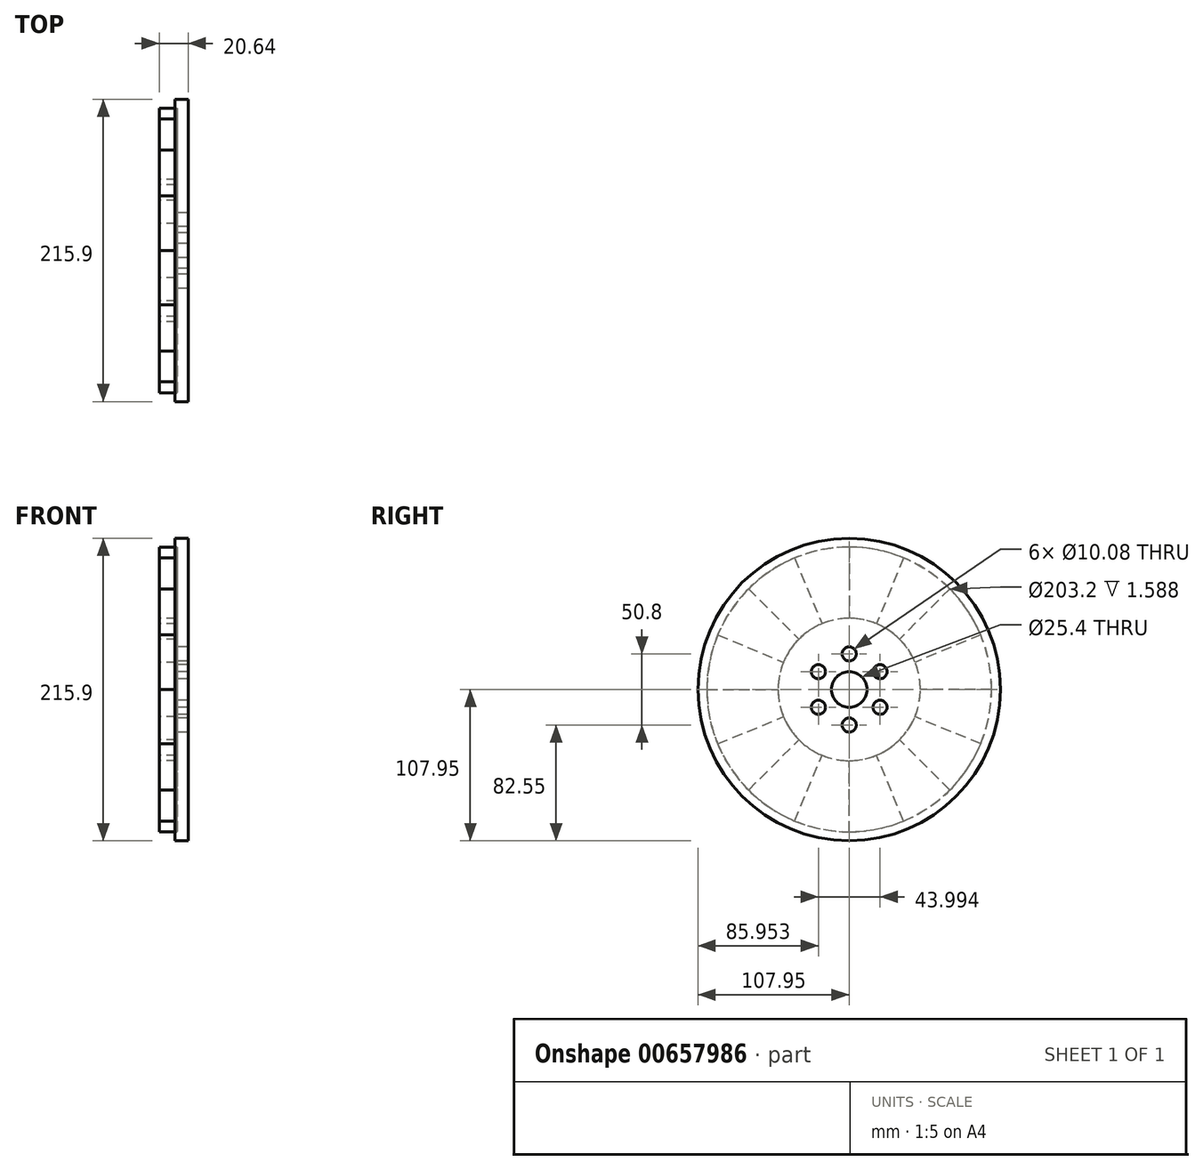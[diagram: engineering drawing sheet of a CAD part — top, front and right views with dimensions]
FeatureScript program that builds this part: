
annotation { "Feature Type Name" : "Feature", "Feature Type Description" : "" }
export const myFeature = defineFeature(function(context is Context, id is Id, definition is map)
    precondition{}
    {
        {
            var Q0;
            Q0=qCreatedBy(makeId("Front.planeOp"),FACE);
            var sketch = newSketch(context, id + "F0", { "sketchPlane" : qUnion([Q0])});
            skLineSegment(sketch, "E0", {"start": v(-9.52, 12.7) * mm, "end": v(0, 12.7) * mm});
            skLineSegment(sketch, "E1", {"start": v(0, 12.7) * mm, "end": v(0, 107.95) * mm});
            skLineSegment(sketch, "E2", {"start": v(0, 107.95) * mm, "end": v(-9.52, 107.95) * mm});
            skLineSegment(sketch, "E3", {"start": v(-9.52, 107.95) * mm, "end": v(-9.52, 101.6) * mm});
            skLineSegment(sketch, "E4", {"start": v(-9.52, 101.6) * mm, "end": v(-7.94, 101.6) * mm});
            skLineSegment(sketch, "E5", {"start": v(-7.94, 101.6) * mm, "end": v(-7.94, 50.8) * mm});
            skLineSegment(sketch, "E6", {"start": v(-7.94, 50.8) * mm, "end": v(-9.52, 50.8) * mm});
            skLineSegment(sketch, "E7", {"start": v(-9.52, 50.8) * mm, "end": v(-9.52, 12.7) * mm});
            skLineSegment(sketch, "E8", {"start": v(-50.8, 0) * mm, "end": v(50.8, 0) * mm, "construction": true});
            skLineSegment(sketch, "E9", {"start": v(0, 0) * mm, "end": v(0, 12.7) * mm, "construction": true});
            skLineSegment(sketch, "E10.bottom", {"start": v(-20.64, 101.6) * mm, "end": v(-7.94, 101.6) * mm});
            skLineSegment(sketch, "E10.top", {"start": v(-20.64, 50.8) * mm, "end": v(-7.94, 50.8) * mm});
            skLineSegment(sketch, "E10.left", {"start": v(-20.64, 101.6) * mm, "end": v(-20.64, 50.8) * mm});
            skSolve(sketch);
        }
        {
            var Q0;
            Q0=makeQuery(id+"F0.imprint","IMPRINT",FACE,{"disambiguationData":[TD([[makeQuery(id+"F0.imprint","IMPRINT",EDGE,{"derivedFrom":sQuery(id+"F0.wireOp",EDGE,"E0")}),1.0]])]});
            var Q1;
            Q1=sQuery(id+"F0.wireOp",EDGE,"E8");
            revolve(context, id + "F1", {"entities" : qUnion([Q0]), "axis" : qUnion([Q1]), "revolveType" : RevolveType.FULL});
        }
        {
            var Q0;
            {var subQ3=sQuery(id+"F0.wireOp",EDGE,"E10.left");Q0=makeQuery(id+"F0.imprint","IMPRINT",FACE,{"disambiguationData":[TD([[makeQuery(id+"F0.imprint","IMPRINT",EDGE,{"derivedFrom":subQ3}),1.0]])]});}
            var Q1;
            Q1=sQuery(id+"F0.wireOp",EDGE,"E8");
            revolve(context, id + "F2", {"entities" : qUnion([Q0]), "axis" : qUnion([Q1]), "revolveType" : RevolveType.ONE_DIRECTION, "angle" : 22.5 * degree});
        }
        {
            var Q0;
            Q0=makeQuery(id+"F2.opRevolve","SWEPT_BODY",BODY,{"disambiguationData":[OSD([sQuery(id+"F0.wireOp",EDGE,"E10.bottom"),sQuery(id+"F0.wireOp",EDGE,"E10.top"),sQuery(id+"F0.wireOp",EDGE,"E10.left"),sQuery(id+"F0.wireOp",EDGE,"E5")])]});
            var Q1;
            Q1=sQuery(id+"F0.wireOp",EDGE,"E8");
            circularPattern(context, id + "F3", {"entities" : qUnion([Q0]), "axis" : qUnion([Q1]), "angle" : 360 * degree, "instanceCount" : 16, "equalSpace" : true});
        }
        {
            var Q0;
            Q0=makeQuery(id+"F1.opRevolve","SWEPT_FACE",FACE,{"disambiguationData":[OSD([sQuery(id+"F0.wireOp",EDGE,"E7")])]});
            var sketch = newSketch(context, id + "F4", { "sketchPlane" : qUnion([Q0])});
            skCircle(sketch, "E11.cCircle", {"center": v(0, 0) * mm, "radius": 25.4 * mm, "construction": true});
            skLineSegment(sketch, "E11.0", {"start": v(0, 25.4) * mm, "end": v(22, 12.7) * mm, "construction": true});
            skLineSegment(sketch, "E11.1", {"start": v(22, 12.7) * mm, "end": v(22, -12.7) * mm, "construction": true});
            skLineSegment(sketch, "E11.2", {"start": v(22, -12.7) * mm, "end": v(0, -25.4) * mm, "construction": true});
            skLineSegment(sketch, "E11.3", {"start": v(0, -25.4) * mm, "end": v(-22, -12.7) * mm, "construction": true});
            skLineSegment(sketch, "E11.4", {"start": v(-22, -12.7) * mm, "end": v(-22, 12.7) * mm, "construction": true});
            skLineSegment(sketch, "E11.5", {"start": v(-22, 12.7) * mm, "end": v(0, 25.4) * mm, "construction": true});
            skSolve(sketch);
        }
        {
            var Q0;
            Q0=sQuery(id+"F4.wireOp",VERTEX,"E11.0.start");
            var Q1;
            Q1=sQuery(id+"F4.wireOp",VERTEX,"E11.5.start");
            var Q2;
            Q2=sQuery(id+"F4.wireOp",VERTEX,"E11.4.start");
            var Q3;
            Q3=sQuery(id+"F4.wireOp",VERTEX,"E11.3.start");
            var Q4;
            Q4=sQuery(id+"F4.wireOp",VERTEX,"E11.2.start");
            var Q5;
            Q5=sQuery(id+"F4.wireOp",VERTEX,"E11.1.start");
            var Q6;
            Q6=makeQuery(id+"F1.opRevolve","SWEPT_BODY",BODY,{"disambiguationData":[OSD([sQuery(id+"F0.wireOp",EDGE,"E0"),sQuery(id+"F0.wireOp",EDGE,"E1"),sQuery(id+"F0.wireOp",EDGE,"E2"),sQuery(id+"F0.wireOp",EDGE,"E3"),sQuery(id+"F0.wireOp",EDGE,"E7"),sQuery(id+"F0.wireOp",EDGE,"E10.bottom"),sQuery(id+"F0.wireOp",EDGE,"E10.top"),sQuery(id+"F0.wireOp",EDGE,"E5")])]});
            hole(context, id + "F5", {"style" : HoleStyle.SIMPLE, "endStyle" : HoleEndStyle.THROUGH, "standardTappedOrClearance" : lookupTablePath({ "standard" : "ANSI", "fit" : "Normal (ASME)", "size" : "3/8", "type" : "Clearance" }), "standardBlindInLast" : lookupTablePath({ "fit" : "Free", "standard" : "ANSI", "size" : "3/8", "type" : "Clearance" }), "holeDiameter" : 10.08 * mm, "majorDiameter" : 6.35 * mm, "isTappedThrough" : true, "tappedDepth" : 12.7 * mm, "tapClearance" : 3, "locations" : qUnion([Q0, Q1, Q2, Q3, Q4, Q5]), "scope" : qUnion([Q6])});
        }
    });
